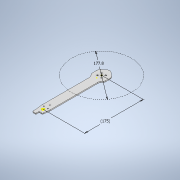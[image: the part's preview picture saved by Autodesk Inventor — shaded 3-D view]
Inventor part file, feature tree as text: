
AUTODESK INVENTOR PART (.ipt)
format: ipt  version: 2020 (Build 240168000, 168)  size: 227,840 bytes
history: native  units: in
note: dims shown in document units (in); Inventor stores cm internally (conversion verified against a paired STEP export)
features: sketch x3, extrude x2, fillet x1
ambient origin geometry x8: Origin, YZ Plane, XZ Plane, XY Plane, X Axis, Y Axis, Z Axis, Center Point
bodies: Body1 (feature_tree)
feature tree (6):
  extrude  "Extrusion1"  Depth=0.1181in
  sketch  "Sketch4"  dims[d7=0.4724in d9=7.0in d10=6.8898in]
  extrude  "Extrusion2"  Depth=7.0in
  fillet  "Fillet1"  Radius=6.8898in
  sketch  "Sketch3"  dims[d2=0.1181in d3=0.0in d4=0.8352in]
  sketch  "Sketch5"  dims[d11=6.8898in d12=0.2953in d13=0.2953in d14=0.9835in d15=0.9835in d16=0.9835in d17=0.1181in d18=0.0in d19=0.3937in]
